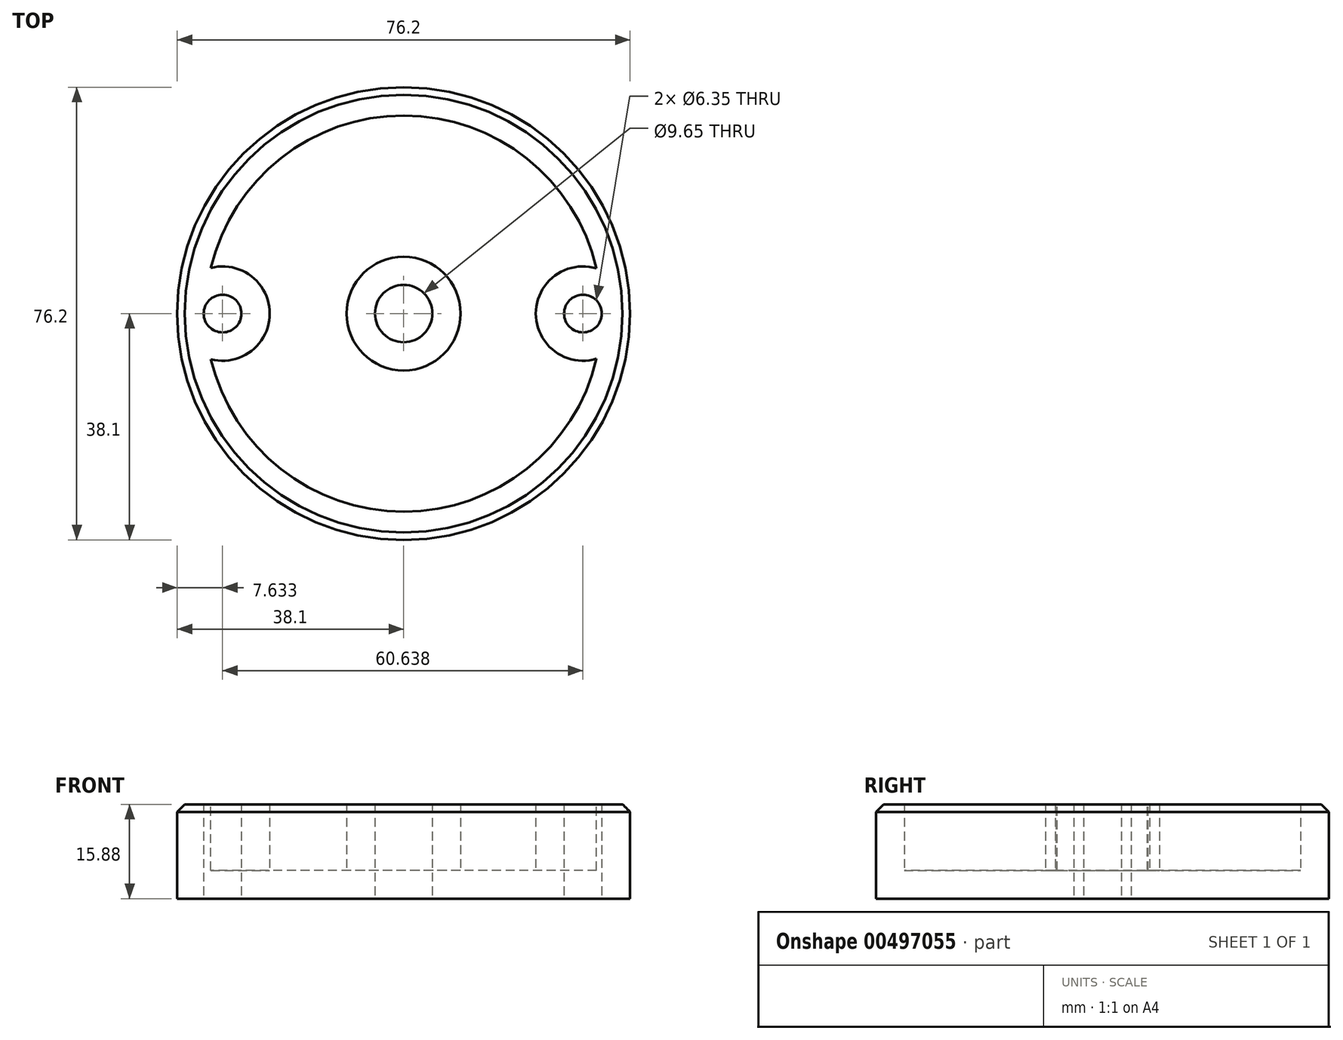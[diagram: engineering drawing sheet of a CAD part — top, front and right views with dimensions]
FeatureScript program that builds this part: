
annotation { "Feature Type Name" : "Feature", "Feature Type Description" : "" }
export const myFeature = defineFeature(function(context is Context, id is Id, definition is map)
    precondition{}
    {
        {
            var Q0;
            Q0=qCreatedBy(makeId("Top.planeOp"),FACE);
            var sketch = newSketch(context, id + "F0", { "sketchPlane" : qUnion([Q0])});
            skCircle(sketch, "E0", {"center": v(0, 0) * mm, "radius": 38.1 * mm});
            skCircle(sketch, "E1.0", {"center": v(0, 0) * mm, "radius": 4.83 * mm});
            skCircle(sketch, "E2", {"center": v(-30.47, 0) * mm, "radius": 3.18 * mm});
            skCircle(sketch, "E3", {"center": v(30.17, 0) * mm, "radius": 3.18 * mm});
            skSolve(sketch);
        }
        {
            var Q0;
            Q0=makeQuery(id+"F0.imprint","IMPRINT",FACE,{"disambiguationData":[TD([[makeQuery(id+"F0.imprint","IMPRINT",EDGE,{"derivedFrom":sQuery(id+"F0.wireOp",EDGE,"E0")}),1.0]])]});
            extrude(context, id + "F1", {"entities" : qUnion([Q0]), "depth" : 15.88 * mm});
        }
        {
            var Q0;
            Q0=makeQuery(id+"F1.opExtrude","CAP_FACE",FACE,{"disambiguationData":[OSD([sQuery(id+"F0.wireOp",EDGE,"E0"),sQuery(id+"F0.wireOp",EDGE,"E1.0")])],"isStart":false});
            shell(context, id + "F2", {"entities" : qUnion([Q0]), "thickness" : 4.76 * mm});
        }
        {
            var Q0;
            Q0=makeQuery(id+"F1.opExtrude","CAP_EDGE",EDGE,{"disambiguationData":[OSD([sQuery(id+"F0.wireOp",EDGE,"E0")])],"isStart":false});
            chamfer(context, id + "F3", {"entities" : qUnion([Q0]), "width" : 1.27 * mm, "tangentPropagation" : true});
        }
    });
